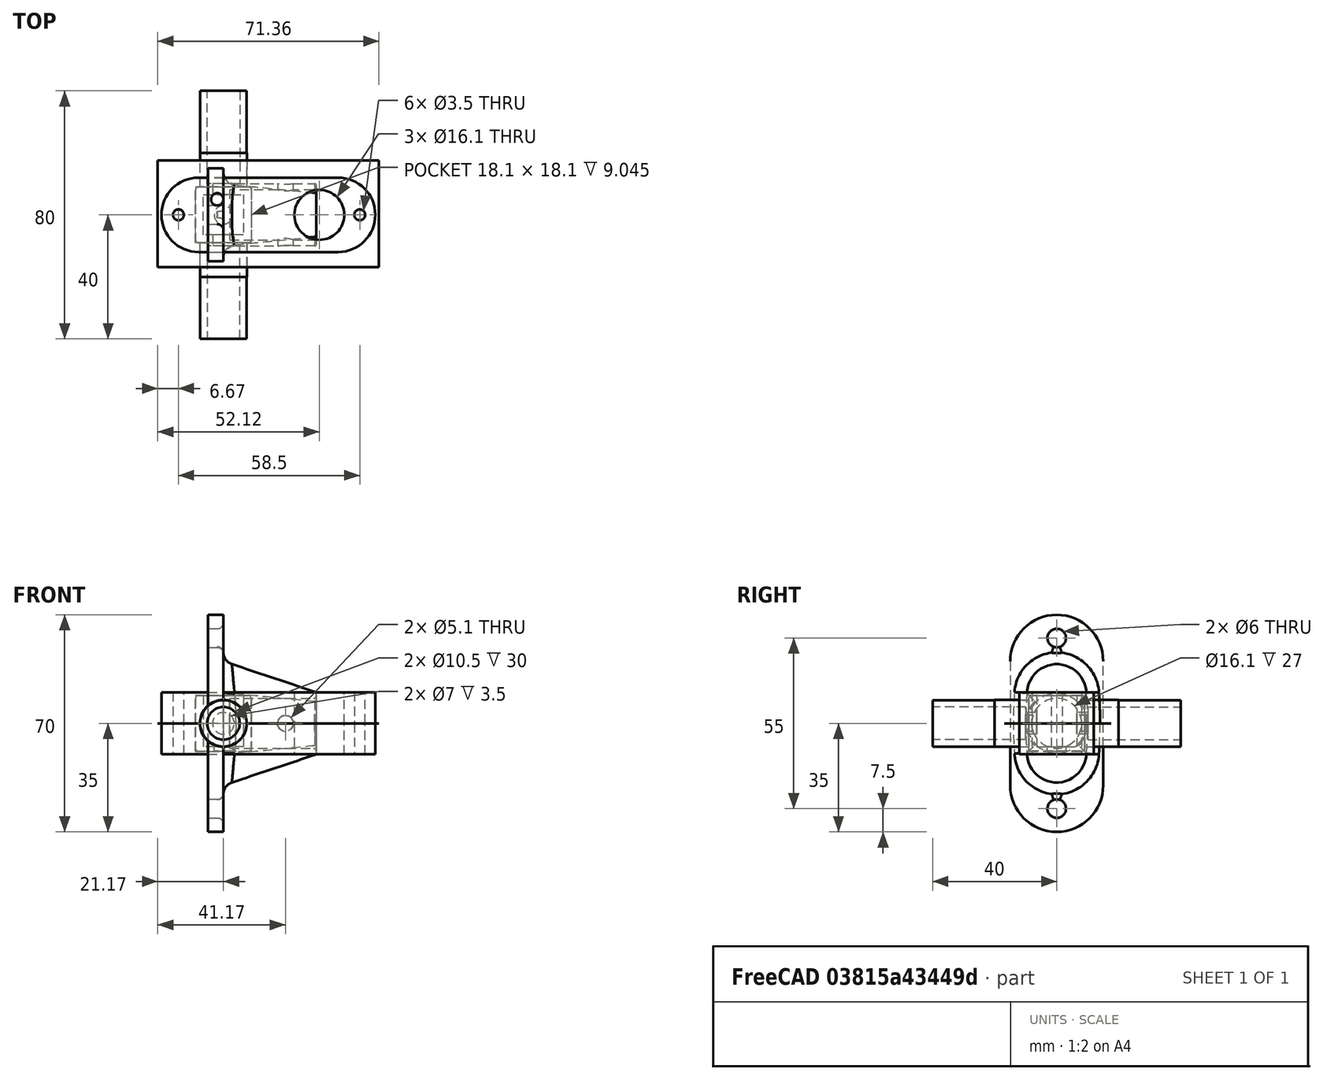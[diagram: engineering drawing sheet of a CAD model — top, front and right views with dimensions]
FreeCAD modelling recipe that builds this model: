
FCSTD DOCUMENT  (FreeCAD 0.20RUnknown)
Label: dipole_antenna_10mm
License: All rights reserved
LicenseURL: http://en.wikipedia.org/wiki/All_rights_reserved
objects: Sketcher::SketchObject×18, PartDesign::Pocket×8, PartDesign::Pad×7, PartDesign::Fillet×5, PartDesign::Body×5, Part::FeaturePython×5, PartDesign::ShapeBinder×2, Mesh::Feature×1, PartDesign::Boolean×1, App::DocumentObjectGroup×1, PartDesign::AdditiveLoft×1
note: 73 computed .brp shape members not serialized (recipe doc carries the construction recipe); baked Part::Feature solids carry a one-line shape summary decoded from their .brp

FEATURE [Mesh::Feature] body
  Placement = pos=(-80,-113,0) rot=(0,0,1;0rad)
FEATURE [Sketcher::SketchObject] Sketch
  FullyConstrained = true
  MapMode = 5
  Placement = pos=(0,0,0) rot=(1,0,0;1.5708rad)
  Support = -> [XZ_Plane]
  sketch-geometry (1):
    g0: Circle CenterX=0 CenterY=0 CenterZ=0 NormalX=0 NormalY=0 NormalZ=1 AngleXU=0 Radius=7.5
  constraints (2):
    c: Diameter(g0) = 15
    c: Coincident(g0,g-1)
FEATURE [PartDesign::Pad] Pad  label="outer_tube_pad"
  Direction = (0,-1,2e-16)
  Length = 80
  Length2 = 10
  Midplane = true
  Placement = pos=(0,0,0) rot=(1,0,0;1.5708rad)
  Profile = -> Sketch
  ReferenceAxis = -> Sketch [N_Axis]
  Type = 0
FEATURE [Sketcher::SketchObject] Sketch001
  AttachmentOffset = pos=(0,0,40) rot=(0,0,1;0rad)
  FullyConstrained = true
  MapMode = 5
  Placement = pos=(0,-40,-8.9e-15) rot=(1,0,0;1.5708rad)
  Support = -> [XZ_Plane]
  sketch-geometry (1):
    g0: Circle CenterX=0 CenterY=0 CenterZ=0 NormalX=0 NormalY=0 NormalZ=1 AngleXU=0 Radius=5.25
  constraints (2):
    c: Coincident(g0,g-1)
    c: Diameter(g0) = 10.5
FEATURE [PartDesign::Pocket] Pocket  label="tube_inset_1_pocket"
  BaseFeature = -> Pad
  Direction = (0,1,-2e-16)
  Length = 30
  Length2 = 5
  Placement = pos=(0,0,0) rot=(1,0,0;1.5708rad)
  Profile = -> Sketch001
  ReferenceAxis = -> Sketch001 [N_Axis]
  Type = 0
FEATURE [Sketcher::SketchObject] Sketch002  label="Inner tube sketch"
  AttachmentOffset = pos=(0,0,-40) rot=(0,0,1;0rad)
  FullyConstrained = true
  MapMode = 5
  Placement = pos=(0,40,8.9e-15) rot=(1,0,0;1.5708rad)
  Support = -> [XZ_Plane]
  sketch-geometry (1):
    g0: Circle CenterX=0 CenterY=0 CenterZ=0 NormalX=0 NormalY=0 NormalZ=1 AngleXU=0 Radius=5.25
  constraints (2):
    c: Coincident(g0,g-1)
    c: Diameter(g0) = 10.5
FEATURE [PartDesign::Pocket] Pocket001  label="tube_inset_2_pocket"
  BaseFeature = -> Pocket
  Direction = (0,1,-2e-16)
  Length = 30
  Length2 = 5
  Placement = pos=(0,0,0) rot=(1,0,0;1.5708rad)
  Profile = -> Sketch002
  ReferenceAxis = -> Sketch002 [N_Axis]
  Reversed = true
  Type = 0
FEATURE [Sketcher::SketchObject] Sketch004
  FullyConstrained = true
  MapMode = 5
  Placement = pos=(0,0,0) rot=(0.57735,0.57735,0.57735;2.0944rad)
  Support = -> [YZ_Plane]
  sketch-geometry (4):
    g0: LineSegment StartX=-9 StartY=9 StartZ=0 EndX=9 EndY=9 EndZ=0
    g1: LineSegment StartX=9 StartY=9 StartZ=0 EndX=9 EndY=-9 EndZ=0
    g2: LineSegment StartX=9 StartY=-9 StartZ=0 EndX=-9 EndY=-9 EndZ=0
    g3: LineSegment StartX=-9 StartY=-9 StartZ=0 EndX=-9 EndY=9 EndZ=0
  constraints (11):
    c: Coincident(g0,g1)
    c: Coincident(g1,g2)
    c: Coincident(g2,g3)
    c: Coincident(g3,g0)
    c: Horizontal(g0)
    c: Horizontal(g2)
    c: Vertical(g1)
    c: Vertical(g3)
    c: Symmetric(g0,g2,g-1)
    c: DistanceX(g0,g0) = 18
    c: Equal(g0,g1)
FEATURE [PartDesign::Pad] Pad001  label="middle_base_pad"
  BaseFeature = -> Pocket001
  Direction = (1,-2e-16,3e-16)
  Length = 18
  Length2 = 10
  Midplane = true
  Placement = pos=(0,0,0) rot=(1,0,0;1.5708rad)
  Profile = -> Sketch004
  ReferenceAxis = -> Sketch004 [N_Axis]
  Type = 0
FEATURE [Sketcher::SketchObject] Sketch005
  FullyConstrained = true
  MapMode = 5
  Placement = pos=(0,0,0) rot=(1,0,0;1.5708rad)
  Support = -> [XZ_Plane]
  sketch-geometry (1):
    g0: Circle CenterX=0 CenterY=0 CenterZ=0 NormalX=0 NormalY=0 NormalZ=1 AngleXU=0 Radius=3.5
  constraints (2):
    c: Coincident(g0,g-1)
    c: Diameter(g0) = 7
FEATURE [PartDesign::Pocket] Pocket002  label="pocket_all_through"
  BaseFeature = -> Pad001
  Direction = (0,1,-2e-16)
  Length = 5
  Length2 = 5
  Midplane = true
  Placement = pos=(0,0,0) rot=(1,0,0;1.5708rad)
  Profile = -> Sketch005
  ReferenceAxis = -> Sketch005 [N_Axis]
  Type = 1
FEATURE [Sketcher::SketchObject] Sketch006
  FullyConstrained = true
  MapMode = 5
  Support = -> [XY_Plane]
  sketch-geometry (1):
    g0: Circle CenterX=0 CenterY=0 CenterZ=0 NormalX=0 NormalY=0 NormalZ=1 AngleXU=0 Radius=3
  constraints (2):
    c: Coincident(g0,g-1)
    c: Diameter(g0) = 6
FEATURE [PartDesign::Pocket] Pocket003  label="sma_pocket"
  BaseFeature = -> Pocket002
  Direction = (0,0,-1)
  Length = 5
  Length2 = 5
  Midplane = true
  Placement = pos=(0,0,0) rot=(1,0,0;1.5708rad)
  Profile = -> Sketch006
  ReferenceAxis = -> Sketch006 [N_Axis]
  Type = 1
FEATURE [Sketcher::SketchObject] Sketch008
  AttachmentOffset = pos=(0,0,9) rot=(0,0,1;0rad)
  FullyConstrained = true
  MapMode = 5
  Placement = pos=(0,0,9) rot=(0,0,1;0rad)
  Support = -> [XY_Plane]
  sketch-geometry (4):
    g0: LineSegment StartX=-6.5 StartY=6.5 StartZ=0 EndX=6.5 EndY=6.5 EndZ=0
    g1: LineSegment StartX=6.5 StartY=6.5 StartZ=0 EndX=6.5 EndY=-6.5 EndZ=0
    g2: LineSegment StartX=6.5 StartY=-6.5 StartZ=0 EndX=-6.5 EndY=-6.5 EndZ=0
    g3: LineSegment StartX=-6.5 StartY=-6.5 StartZ=0 EndX=-6.5 EndY=6.5 EndZ=0
  constraints (11):
    c: Coincident(g0,g1)
    c: Coincident(g1,g2)
    c: Coincident(g2,g3)
    c: Coincident(g3,g0)
    c: Horizontal(g0)
    c: Horizontal(g2)
    c: Vertical(g1)
    c: Vertical(g3)
    c: Symmetric(g0,g2,g-1)
    c: DistanceY(g1,g1) = 13
    c: Equal(g1,g0)
FEATURE [PartDesign::Pocket] Pocket004
  BaseFeature = -> Pocket003
  Direction = (0,0,-1)
  Length = 16.5
  Length2 = 5
  Placement = pos=(0,0,0) rot=(1,0,0;1.5708rad)
  Profile = -> Sketch008
  ReferenceAxis = -> Sketch008 [N_Axis]
  Type = 0
FEATURE [PartDesign::Fillet] Fillet
  Base = -> Pocket004 [Edge18,Edge22,Edge8,Edge20,Edge7,Edge21,Edge13,Edge6,Edge19,Edge12,Edge5,Edge11]
  BaseFeature = -> Pocket004
  Placement = pos=(0,0,0) rot=(1,0,0;1.5708rad)
  Radius = 1
  SupportTransform = false
  UseAllEdges = false
FEATURE [PartDesign::Body] Body  label="antenna_core"
  Group = -> [Sketch,Pad,Sketch001,Pocket,Sketch002,Pocket001,Sketch004,Pad001,Sketch005,Pocket002,Sketch006,Pocket003,Sketch008,Pocket004,Fillet]
  Origin = -> Origin
  Tip = -> Fillet
FEATURE [Sketcher::SketchObject] Sketch009
  FullyConstrained = true
  MapMode = 5
  Support = -> [XY_Plane001]
  sketch-geometry (15):
    g0: Circle CenterX=30.95 CenterY=0 CenterZ=0 NormalX=0 NormalY=0 NormalZ=1 AngleXU=0 Radius=8.05
    g1: ArcOfCircle CenterX=-8 CenterY=0 CenterZ=0 NormalX=0 NormalY=0 NormalZ=1 AngleXU=0 Radius=12 StartAngle=1.5708 EndAngle=4.71239
    g2: ArcOfCircle CenterX=37 CenterY=0 CenterZ=0 NormalX=0 NormalY=0 NormalZ=1 AngleXU=0 Radius=12 StartAngle=4.71239 EndAngle=7.85398
    g3: LineSegment StartX=-8 StartY=-12 StartZ=0 EndX=37 EndY=-12 EndZ=0
    g4: LineSegment StartX=37 StartY=12 StartZ=0 EndX=-8 EndY=12 EndZ=0
    g5: Circle CenterX=-14.5 CenterY=0 CenterZ=0 NormalX=0 NormalY=0 NormalZ=1 AngleXU=0 Radius=1.75
    g6: Circle CenterX=44 CenterY=0 CenterZ=0 NormalX=0 NormalY=0 NormalZ=1 AngleXU=0 Radius=1.75
    g7: LineSegment StartX=-9 StartY=9 StartZ=0 EndX=9 EndY=9 EndZ=0
    g8: LineSegment StartX=9 StartY=9 StartZ=0 EndX=9 EndY=-9 EndZ=0
    g9: LineSegment StartX=9 StartY=-9 StartZ=0 EndX=-9 EndY=-9 EndZ=0
    g10: LineSegment StartX=-9 StartY=-9 StartZ=0 EndX=-9 EndY=9 EndZ=0
    g11: GeomPoint X=-20 Y=0 Z=0
    g12: GeomPoint X=-9 Y=0 Z=0
    g13: GeomPoint X=39 Y=0 Z=0
    g14: GeomPoint X=49 Y=0 Z=0
  constraints (36):
    c: PointOnObject(g0,g-1)
    c: Diameter(g0) = 16.1
    c: Tangent(g1,g3) = -1.5708
    c: Tangent(g3,g2) = -1.5708
    c: Tangent(g2,g4) = -1.5708
    c: Tangent(g4,g1) = -1.5708
    c: Equal(g1,g2)
    c: PointOnObject(g1,g-1)
    c: PointOnObject(g2,g-1)
    c: PointOnObject(g5,g-1)
    c: PointOnObject(g6,g-1)
    c: Diameter(g6) = 3.5
    c: Equal(g6,g5)
    c: DistanceY(g2,g2) = 24
    c: Coincident(g7,g8)
    c: Coincident(g8,g9)
    c: Coincident(g9,g10)
    c: Coincident(g10,g7)
    c: Horizontal(g7)
    c: Horizontal(g9)
    c: Vertical(g8)
    c: Vertical(g10)
    c: Symmetric(g7,g9,g-1)
    c: DistanceY(g8,g8) = 18
    c: Equal(g8,g7)
    c: PointOnObject(g11,g1)
    c: PointOnObject(g11,g-1)
    c: PointOnObject(g12,g10)
    c: Symmetric(g11,g12,g5)
    c: PointOnObject(g13,g0)
    c: PointOnObject(g13,g-1)
    c: PointOnObject(g14,g2)
    c: Symmetric(g14,g13,g6)
    c: DistanceX(g1,g2) = 45
    c: DistanceX(g13,g14) = 10
    c: DistanceX(g11,g-1) = 20
FEATURE [Sketcher::SketchObject] Sketch010
  FullyConstrained = true
  MapMode = 5
  Support = -> [XY_Plane002]
  sketch-geometry (4):
    g0: LineSegment StartX=-9.05 StartY=9.05 StartZ=0 EndX=9.05 EndY=9.05 EndZ=0
    g1: LineSegment StartX=9.05 StartY=9.05 StartZ=0 EndX=9.05 EndY=-9.05 EndZ=0
    g2: LineSegment StartX=9.05 StartY=-9.05 StartZ=0 EndX=-9.05 EndY=-9.05 EndZ=0
    g3: LineSegment StartX=-9.05 StartY=-9.05 StartZ=0 EndX=-9.05 EndY=9.05 EndZ=0
  constraints (11):
    c: Coincident(g0,g1)
    c: Coincident(g1,g2)
    c: Coincident(g2,g3)
    c: Coincident(g3,g0)
    c: Horizontal(g0)
    c: Horizontal(g2)
    c: Vertical(g1)
    c: Vertical(g3)
    c: Symmetric(g0,g2,g-1)
    c: DistanceY(g1,g1) = 18.1
    c: Equal(g1,g2)
FEATURE [PartDesign::Pad] Pad002
  Direction = (0,0,1)
  Length = 18.1
  Length2 = 10
  Midplane = true
  Profile = -> Sketch010
  ReferenceAxis = -> Sketch010 [N_Axis]
  Type = 0
FEATURE [Sketcher::SketchObject] Sketch011
  FullyConstrained = true
  MapMode = 5
  Placement = pos=(0,0,0) rot=(1,0,0;1.5708rad)
  Support = -> [XZ_Plane]
  sketch-geometry (1):
    g0: Circle CenterX=0 CenterY=0 CenterZ=0 NormalX=0 NormalY=0 NormalZ=1 AngleXU=0 Radius=7.55
  constraints (2):
    c: Coincident(g0,g-1)
    c: Diameter(g0) = 15.1
FEATURE [PartDesign::Pad] Pad003
  BaseFeature = -> Pad002
  Direction = (0,-1,2e-16)
  Length = 40
  Length2 = 10
  Midplane = true
  Profile = -> Sketch011
  ReferenceAxis = -> Sketch011 [N_Axis]
  Type = 0
FEATURE [PartDesign::Body] Body002  label="antenna_core_outline"
  Group = -> [Sketch010,Pad002,Sketch011,Pad003]
  Origin = -> Origin002
  Tip = -> Pad003
FEATURE [PartDesign::Pad] Pad004
  Direction = (0,0,1)
  Length = 20
  Length2 = 10
  Midplane = true
  Profile = -> Sketch009
  ReferenceAxis = -> Sketch009 [N_Axis]
  Type = 0
FEATURE [PartDesign::Boolean] Boolean
  BaseFeature = -> Pad004
  Group = -> [Body002]
  Type = 1
FEATURE [PartDesign::Body] Body001  label="holder"
  Group = -> [Sketch009,Pad004,Boolean]
  Origin = -> Origin001
  Tip = -> Boolean
FEATURE [Sketcher::SketchObject] Sketch013
  FullyConstrained = false
  MapMode = 5
  Support = -> [XY_Plane003]
  sketch-geometry (4):
    g0: LineSegment StartX=-21.1721 StartY=17.5791 StartZ=0 EndX=50.1851 EndY=17.5791 EndZ=0
    g1: LineSegment StartX=50.1851 StartY=17.5791 StartZ=0 EndX=50.1851 EndY=-16.8597 EndZ=0
    g2: LineSegment StartX=50.1851 StartY=-16.8597 StartZ=0 EndX=-21.1721 EndY=-16.8597 EndZ=0
    g3: LineSegment StartX=-21.1721 StartY=-16.8597 StartZ=0 EndX=-21.1721 EndY=17.5791 EndZ=0
  constraints (8):
    c: Coincident(g0,g1)
    c: Coincident(g1,g2)
    c: Coincident(g2,g3)
    c: Coincident(g3,g0)
    c: Horizontal(g0)
    c: Horizontal(g2)
    c: Vertical(g1)
    c: Vertical(g3)
FEATURE [PartDesign::Pad] Pad005
  Direction = (0,0,1)
  Length = 0.01
  Length2 = 10
  Midplane = true
  Profile = -> Sketch013
  ReferenceAxis = -> Sketch013 [N_Axis]
  Type = 0
FEATURE [PartDesign::ShapeBinder] CopySlice_child0
  Placement = pos=(0,0,-10) rot=(0,0,1;0rad)
  TraceSupport = false
FEATURE [PartDesign::ShapeBinder] CopySlice_child0001
  Placement = pos=(0,0,-10) rot=(0,0,1;0rad)
  TraceSupport = false
FEATURE [Sketcher::SketchObject] Sketch014
  FullyConstrained = true
  MapMode = 5
  Support = -> [XY_Plane003]
  sketch-geometry (1):
    g0: Circle CenterX=0 CenterY=0 CenterZ=0 NormalX=0 NormalY=0 NormalZ=1 AngleXU=0 Radius=4.5
  constraints (2):
    c: Coincident(g0,g-1)
    c: Diameter(g0) = 9
FEATURE [PartDesign::Body] Body003  label="holder_split"
  Group = -> [Sketch013,Pad005,CopySlice_child0,CopySlice_child0001,Sketch014]
  Origin = -> Origin003
  Tip = -> Pad005
FEATURE [Part::FeaturePython] Slice  # WARN: FeaturePython — macro-defined, semantics opaque (R4)
  Base = -> Body001
  Mode = 1
  Tolerance = 0
  Tools = -> [Body003]
FEATURE [Part::FeaturePython] Slice_child0  label="Slice.0"  # WARN: FeaturePython — macro-defined, semantics opaque (R4)
  Base = -> Slice
  FilterType = 1
  Invert = false
  OverrideMaxVal = 0
  WindowFrom = 80
  WindowTo = 100
  items = 0
FEATURE [Part::FeaturePython] Slice_child1  label="Slice.1"  # WARN: FeaturePython — macro-defined, semantics opaque (R4)
  Base = -> Slice
  FilterType = 1
  Invert = false
  OverrideMaxVal = 0
  WindowFrom = 80
  WindowTo = 100
  items = 1
FEATURE [Part::FeaturePython] Slice_child2  label="Slice.2"  # WARN: FeaturePython — macro-defined, semantics opaque (R4)
  Base = -> Slice
  FilterType = 1
  Invert = false
  OverrideMaxVal = 0
  WindowFrom = 80
  WindowTo = 100
  items = 2
FEATURE [Part::FeaturePython] Slice_child3  label="Slice.3"  # WARN: FeaturePython — macro-defined, semantics opaque (R4)
  Base = -> Slice
  FilterType = 1
  Invert = false
  OverrideMaxVal = 0
  WindowFrom = 80
  WindowTo = 100
  items = 3
FEATURE [App::DocumentObjectGroup] GrExplode_Slice  label="Exploded Slice"
  Group = -> [Slice_child0,Slice_child1,Slice_child2,Slice_child3]
FEATURE [Sketcher::SketchObject] Sketch015
  FullyConstrained = true
  MapMode = 5
  Placement = pos=(0,0,0) rot=(0.57735,0.57735,0.57735;2.0944rad)
  Support = -> [YZ_Plane004]
  expr: Constraints[8] = Sketch016.Constraints[1]
  sketch-geometry (5):
    g0: ArcOfCircle CenterX=0 CenterY=10 CenterZ=0 NormalX=0 NormalY=0 NormalZ=1 AngleXU=0 Radius=10 StartAngle=2e-16 EndAngle=3.14159
    g1: ArcOfCircle CenterX=0 CenterY=-10 CenterZ=0 NormalX=0 NormalY=0 NormalZ=1 AngleXU=0 Radius=10 StartAngle=3.14159 EndAngle=6.28319
    g2: LineSegment StartX=-10 StartY=10 StartZ=0 EndX=-10 EndY=-10 EndZ=0
    g3: LineSegment StartX=10 StartY=-10 StartZ=0 EndX=10 EndY=10 EndZ=0
    g4: Circle CenterX=0 CenterY=0 CenterZ=0 NormalX=0 NormalY=0 NormalZ=1 AngleXU=0 Radius=10
  constraints (11):
    c: Tangent(g0,g2) = -1.5708
    c: Tangent(g2,g1) = -1.5708
    c: Tangent(g1,g3) = -1.5708
    c: Tangent(g3,g0) = -1.5708
    c: Equal(g0,g1)
    c: PointOnObject(g0,g-2)
    c: Symmetric(g0,g1,g-1)
    c: Coincident(g4,g-1)
    c: Diameter(g4) = 20
    c: Tangent(g2,g4)
    c: DistanceY(g1,g0) = 20
FEATURE [Sketcher::SketchObject] Sketch016
  AttachmentOffset = pos=(0,0,30) rot=(0,0,1;0rad)
  FullyConstrained = true
  MapMode = 5
  Placement = pos=(30,-6.7e-15,6.7e-15) rot=(0.57735,0.57735,0.57735;2.0944rad)
  Support = -> [YZ_Plane004]
  sketch-geometry (1):
    g0: Circle CenterX=0 CenterY=0 CenterZ=0 NormalX=0 NormalY=0 NormalZ=1 AngleXU=0 Radius=10
  constraints (2):
    c: Coincident(g0,g-1)
    c: Diameter(g0) = 20
FEATURE [PartDesign::AdditiveLoft] AdditiveLoft
  Closed = false
  Placement = pos=(0,0,0) rot=(0.57735,0.57735,0.57735;2.0944rad)
  Profile = -> Sketch015
  Ruled = false
  Sections = -> [Sketch016]
FEATURE [Sketcher::SketchObject] Sketch017
  FullyConstrained = true
  MapMode = 5
  Placement = pos=(0,0,0) rot=(0.57735,0.57735,0.57735;2.0944rad)
  Support = -> [YZ_Plane004]
  sketch-geometry (4):
    g0: ArcOfCircle CenterX=0 CenterY=20 CenterZ=0 NormalX=0 NormalY=0 NormalZ=1 AngleXU=0 Radius=15 StartAngle=0 EndAngle=3.14159
    g1: ArcOfCircle CenterX=0 CenterY=-20 CenterZ=0 NormalX=0 NormalY=0 NormalZ=1 AngleXU=0 Radius=15 StartAngle=3.14159 EndAngle=6.28319
    g2: LineSegment StartX=-15 StartY=20 StartZ=0 EndX=-15 EndY=-20 EndZ=0
    g3: LineSegment StartX=15 StartY=-20 StartZ=0 EndX=15 EndY=20 EndZ=0
  constraints (9):
    c: Tangent(g0,g2) = -1.5708
    c: Tangent(g2,g1) = -1.5708
    c: Tangent(g1,g3) = -1.5708
    c: Tangent(g3,g0) = -1.5708
    c: Equal(g0,g1)
    c: PointOnObject(g0,g-2)
    c: Symmetric(g0,g1,g-1)
    c: DistanceX(g0,g0) = 30
    c: DistanceY(g1,g0) = 40
FEATURE [PartDesign::Pad] Pad006
  BaseFeature = -> AdditiveLoft
  Direction = (1,-2e-16,3e-16)
  Length = 5
  Length2 = 10
  Placement = pos=(0,0,0) rot=(0.57735,0.57735,0.57735;2.0944rad)
  Profile = -> Sketch017
  ReferenceAxis = -> Sketch017 [N_Axis]
  Reversed = true
  Type = 0
FEATURE [PartDesign::Fillet] Fillet001
  Base = -> Pad006 [Edge14,Edge13,Edge12,Edge16,Edge15]
  BaseFeature = -> Pad006
  Placement = pos=(0,0,0) rot=(0.57735,0.57735,0.57735;2.0944rad)
  Radius = 4
  SupportTransform = false
  UseAllEdges = false
FEATURE [Sketcher::SketchObject] Sketch018
  FullyConstrained = true
  MapMode = 5
  Placement = pos=(0,0,0) rot=(0.57735,0.57735,0.57735;2.0944rad)
  Support = -> [YZ_Plane004]
  sketch-geometry (2):
    g0: Circle CenterX=0 CenterY=27.5 CenterZ=0 NormalX=0 NormalY=0 NormalZ=1 AngleXU=0 Radius=3
    g1: Circle CenterX=0 CenterY=-27.5 CenterZ=0 NormalX=0 NormalY=0 NormalZ=1 AngleXU=0 Radius=3
  constraints (5):
    c: PointOnObject(g0,g-2)
    c: Diameter(g0) = 6
    c: Equal(g0,g1)
    c: Symmetric(g0,g1,g-1)
    c: DistanceY(g1,g0) = 55
FEATURE [PartDesign::Pocket] Pocket005
  BaseFeature = -> Fillet001
  Direction = (-1,2e-16,-3e-16)
  Length = 5
  Length2 = 5
  Placement = pos=(0,0,0) rot=(0.57735,0.57735,0.57735;2.0944rad)
  Profile = -> Sketch018
  ReferenceAxis = -> Sketch018 [N_Axis]
  Type = 1
FEATURE [PartDesign::Fillet] Fillet002
  Base = -> Pocket005 [Edge6,Edge5]
  BaseFeature = -> Pocket005
  Placement = pos=(0,0,0) rot=(0.57735,0.57735,0.57735;2.0944rad)
  Radius = 2
  SupportTransform = false
  UseAllEdges = false
FEATURE [Sketcher::SketchObject] Sketch019
  AttachmentOffset = pos=(0,0,30) rot=(0,0,1;0rad)
  FullyConstrained = true
  MapMode = 5
  Placement = pos=(30,-6.7e-15,6.7e-15) rot=(0.57735,0.57735,0.57735;2.0944rad)
  Support = -> [YZ_Plane004]
  sketch-geometry (1):
    g0: Circle CenterX=0 CenterY=0 CenterZ=0 NormalX=0 NormalY=0 NormalZ=1 AngleXU=0 Radius=8.05
  constraints (2):
    c: Coincident(g0,g-1)
    c: Diameter(g0) = 16.1
FEATURE [PartDesign::Pocket] Pocket006
  BaseFeature = -> Fillet002
  Direction = (-1,2e-16,-3e-16)
  Length = 28
  Length2 = 5
  Placement = pos=(0,0,0) rot=(0.57735,0.57735,0.57735;2.0944rad)
  Profile = -> Sketch019
  ReferenceAxis = -> Sketch019 [N_Axis]
  Type = 0
FEATURE [PartDesign::Fillet] Fillet003
  Base = -> Pocket006 [Edge62]
  BaseFeature = -> Pocket006
  Placement = pos=(0,0,0) rot=(0.57735,0.57735,0.57735;2.0944rad)
  Radius = 1
  SupportTransform = false
  UseAllEdges = false
FEATURE [PartDesign::Fillet] Fillet004
  Base = -> Fillet003 [Edge6,Edge4,Edge2,Edge3,Edge5]
  BaseFeature = -> Fillet003
  Placement = pos=(0,0,0) rot=(0.57735,0.57735,0.57735;2.0944rad)
  Radius = 0.5
  SupportTransform = false
  UseAllEdges = false
FEATURE [Sketcher::SketchObject] Sketch020
  FullyConstrained = true
  MapMode = 5
  Placement = pos=(0,0,0) rot=(1,0,0;1.5708rad)
  Support = -> [XZ_Plane004]
  sketch-geometry (1):
    g0: Circle CenterX=20 CenterY=0 CenterZ=0 NormalX=0 NormalY=0 NormalZ=1 AngleXU=0 Radius=2.55
  constraints (3):
    c: PointOnObject(g0,g-1)
    c: Diameter(g0) = 5.1
    c: DistanceX(g-1,g0) = 20
FEATURE [PartDesign::Pocket] Pocket007
  BaseFeature = -> Fillet004
  Direction = (0,1,2e-16)
  Length = 5
  Length2 = 5
  Midplane = true
  Placement = pos=(0,0,0) rot=(0.57735,0.57735,0.57735;2.0944rad)
  Profile = -> Sketch020
  ReferenceAxis = -> Sketch020 [N_Axis]
  Type = 1
FEATURE [PartDesign::Body] Body004  label="wall_mount"
  Group = -> [Sketch015,Sketch016,AdditiveLoft,Sketch017,Pad006,Fillet001,Sketch018,Pocket005,Fillet002,Sketch019,Pocket006,Fillet003,Fillet004,Sketch020,Pocket007]
  Origin = -> Origin004
  Tip = -> Pocket007
